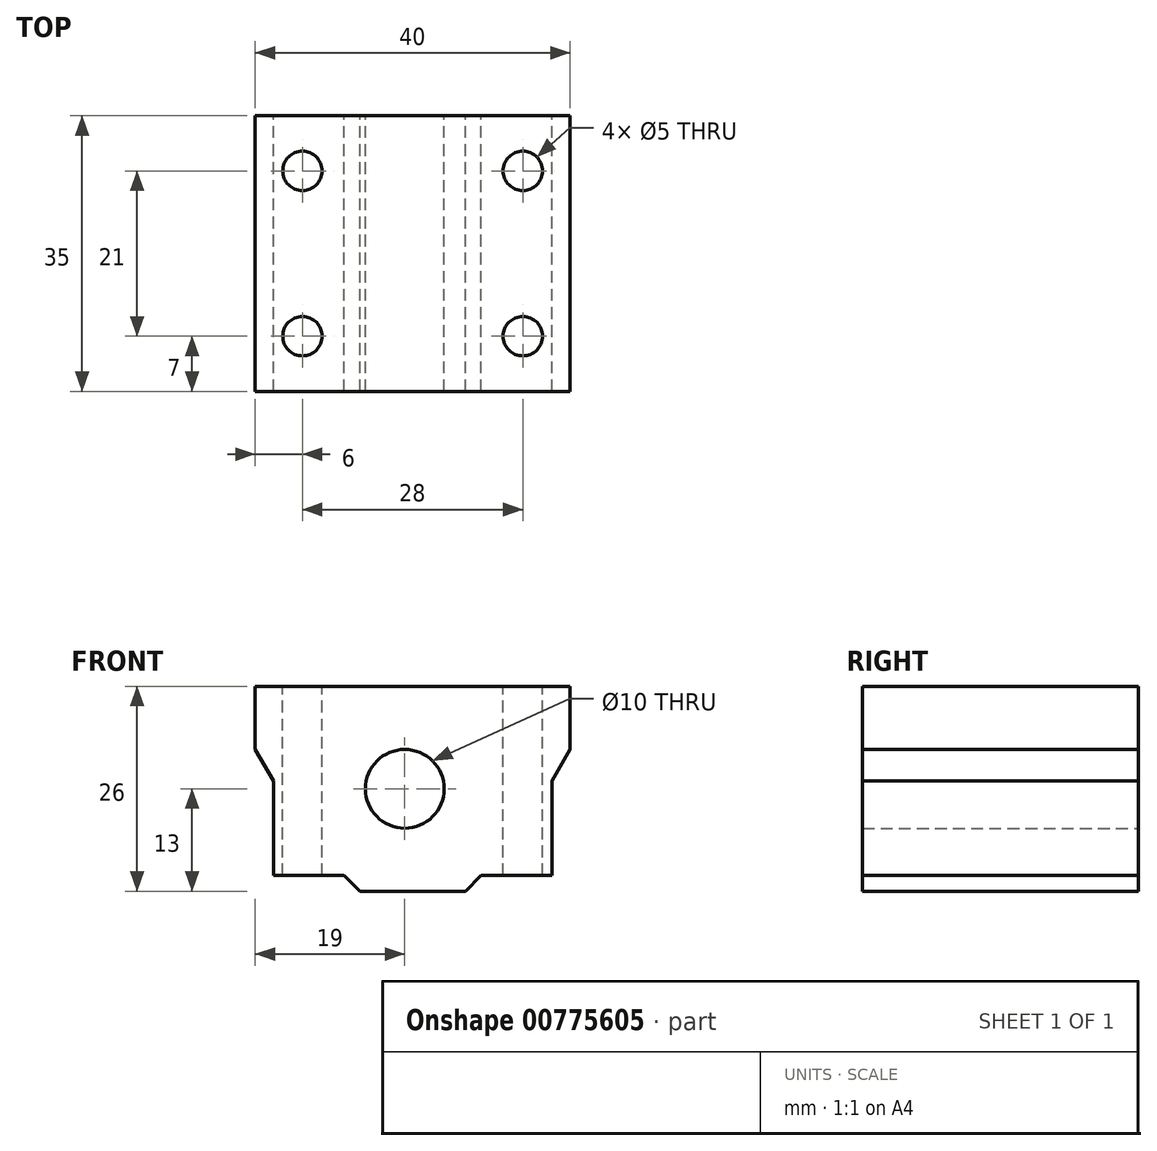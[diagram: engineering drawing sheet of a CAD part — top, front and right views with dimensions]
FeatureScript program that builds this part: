
annotation { "Feature Type Name" : "Feature", "Feature Type Description" : "" }
export const myFeature = defineFeature(function(context is Context, id is Id, definition is map)
    precondition{}
    {
        {
            var Q0;
            Q0=qCreatedBy(makeId("Front.planeOp"),FACE);
            var sketch = newSketch(context, id + "F0", { "sketchPlane" : qUnion([Q0])});
            skLineSegment(sketch, "E0", {"start": v(6.7, -13) * mm, "end": v(-6.7, -13) * mm});
            skLineSegment(sketch, "E1", {"start": v(-6.7, -13) * mm, "end": v(-8.7, -11) * mm});
            skLineSegment(sketch, "E2", {"start": v(-8.7, -11) * mm, "end": v(-17.7, -11) * mm});
            skLineSegment(sketch, "E3", {"start": v(17.7, -11) * mm, "end": v(8.7, -11) * mm});
            skLineSegment(sketch, "E4", {"start": v(8.7, -11) * mm, "end": v(6.7, -13) * mm});
            skLineSegment(sketch, "E5", {"start": v(-17.7, -11) * mm, "end": v(-17.7, 1) * mm});
            skLineSegment(sketch, "E6", {"start": v(-17.7, 1) * mm, "end": v(-20, 5) * mm});
            skLineSegment(sketch, "E7", {"start": v(-20, 5) * mm, "end": v(-20, 13) * mm});
            skLineSegment(sketch, "E8", {"start": v(17.7, -11) * mm, "end": v(17.7, 1) * mm});
            skLineSegment(sketch, "E9", {"start": v(17.7, 1) * mm, "end": v(20, 5) * mm});
            skLineSegment(sketch, "E10", {"start": v(20, 5) * mm, "end": v(20, 13) * mm});
            skLineSegment(sketch, "E11", {"start": v(-20, 13) * mm, "end": v(20, 13) * mm});
            skLineSegment(sketch, "E12", {"start": v(0, 13) * mm, "end": v(0, -13) * mm});
            skCircle(sketch, "E13", {"center": v(-1, 0) * mm, "radius": 5 * mm});
            skSolve(sketch);
        }
        {
            var Q0;
            Q0 = qSketchRegion(id + "F0", true);
            extrude(context, id + "F1", {"entities" : qUnion([Q0]), "depth" : 35 * mm, "offsetDistance" : 25.4 * mm});
        }
        {
            var Q0;
            Q0=qCreatedBy(makeId("Top.planeOp"),FACE);
            var sketch = newSketch(context, id + "F2", { "sketchPlane" : qUnion([Q0])});
            skCircle(sketch, "E14", {"center": v(14, -28) * mm, "radius": 2.5 * mm});
            skCircle(sketch, "E15", {"center": v(14, -7) * mm, "radius": 2.5 * mm});
            skCircle(sketch, "E16", {"center": v(-14, -7) * mm, "radius": 2.5 * mm});
            skCircle(sketch, "E17", {"center": v(-14, -28) * mm, "radius": 2.5 * mm});
            skSolve(sketch);
        }
        {
            var Q0;
            Q0 = qSketchRegion(id + "F2", true);
            extrude(context, id + "F3", {"entities" : qUnion([Q0]), "operationType" : NewBodyOperationType.REMOVE, "endBound" : BoundingType.SYMMETRIC, "oppositeDirection" : true, "depth" : 50.8 * mm, "offsetDistance" : 25.4 * mm});
        }
    });
